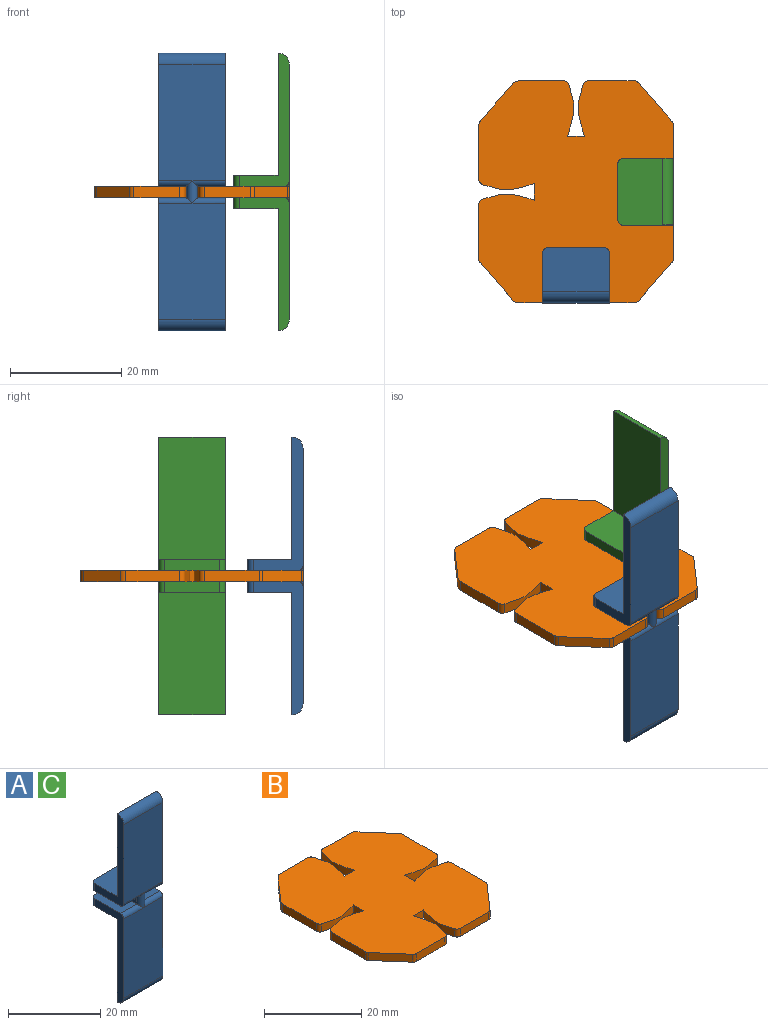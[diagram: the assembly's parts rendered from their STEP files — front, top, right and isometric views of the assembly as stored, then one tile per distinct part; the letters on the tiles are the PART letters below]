
ASSEMBLY  parts=3 mates=2
PART A: 28 faces, bbox 12x10x50 mm
  f0: plane 10x6mm, normal (0,1,0), area 44mm2, adj f2,f4,f5,f8,f10,f17,f18,f19
  f1: plane 21x12mm, normal (0,-1,0), area 252mm2, adj f11,f13,f16,f23,f25
  f2: plane 9x2mm, normal (1,0,0), area 18mm2, adj f0,f4,f8,f15
  f3: plane 21x12mm, normal (0,-1,0), area 252mm2, adj f7,f12,f14,f21,f24
  f4: plane 9x5mm, normal (0,0,-1), area 44.8mm2, adj f0,f2,f7,f14,f18
  f5: plane 12x8mm, normal (0,0,1), area 95.6mm2, adj f0,f6,f7,f18,f21,f27
  f6: plane 22x12mm, normal (0,1,0), area 264mm2, adj f5,f7,f12,f21
  f7: plane 24x9mm, normal (1,0,0), area 60.9mm2, adj f3,f4,f5,f6,f12,f14,f18
  f8: plane 9x5mm, normal (0,0,1), area 44.8mm2, adj f0,f2,f11,f16,f17
  f9: plane 22x12mm, normal (0,1,0), area 264mm2, adj f10,f11,f13,f23
  f10: plane 12x8mm, normal (0,0,-1), area 95.6mm2, adj f0,f9,f11,f17,f23,f26
  f11: plane 24x9mm, normal (1,0,0), area 60.9mm2, adj f1,f8,f9,f10,f13,f16,f17
  f12: cylinder r=2mm len=12mm, axis (-1,0,0), area 37.7mm2, adj f3,f6,f7,f21
  f13: cylinder r=2mm len=12mm, axis (1,0,0), area 37.7mm2, adj f1,f9,f11,f23
  f14: cylinder r=1mm len=6mm, axis (-1,0,0), area 8.4mm2, adj f3,f4,f7,f15
  f15: cylinder r=1mm len=4mm, axis (0,0,1), area 8.6mm2, adj f2,f14,f16,f19,f24,f25
  f16: cylinder r=1mm len=6mm, axis (1,0,0), area 8.4mm2, adj f1,f8,f11,f15
  f17: cylinder r=1mm len=2mm, axis (0,0,-1), area 3.1mm2, adj f0,f8,f10,f11
  f18: cylinder r=1mm len=2mm, axis (0,0,-1), area 3.1mm2, adj f0,f4,f5,f7
  f19: plane 9x2mm, normal (-1,0,0), area 18mm2, adj f0,f15,f20,f22
  f20: plane 9x5mm, normal (0,0,-1), area 44.8mm2, adj f0,f19,f21,f24,f27
  f21: plane 24x9mm, normal (-1,0,0), area 60.9mm2, adj f3,f5,f6,f12,f20,f24,f27
  f22: plane 9x5mm, normal (0,0,1), area 44.8mm2, adj f0,f19,f23,f25,f26
  f23: plane 24x9mm, normal (-1,0,0), area 60.9mm2, adj f1,f9,f10,f13,f22,f25,f26
  f24: cylinder r=1mm len=6mm, axis (1,0,0), area 8.4mm2, adj f3,f15,f20,f21
  f25: cylinder r=1mm len=6mm, axis (-1,0,0), area 8.4mm2, adj f1,f15,f22,f23
  f26: cylinder r=1mm len=2mm, axis (0,0,-1), area 3.1mm2, adj f0,f10,f22,f23
  f27: cylinder r=1mm len=2mm, axis (0,0,-1), area 3.1mm2, adj f0,f5,f20,f21
PART B: 42 faces, bbox 35x40x2 mm
  f0: plane 40x35mm, normal (0,0,-1), area 1233.8mm2, adj f1,f2,f3,f4,f6,f7,f8,f9
  f1: plane 9.85x2mm, normal (1,0,0), area 19.7mm2, adj f0,f5,f17,f36
  f2: plane 8.23x2mm, normal (0,1,0), area 16.5mm2, adj f0,f5,f18,f37
  f3: plane 9.85x2mm, normal (-1,0,0), area 19.7mm2, adj f0,f5,f22,f35
  f4: plane 8.23x2mm, normal (0,-1,0), area 16.5mm2, adj f0,f5,f23,f34
  f5: plane 40x35mm, normal (0,0,1), area 1233.8mm2, adj f1,f2,f3,f4,f6,f7,f8,f9
  f6: plane 9.67x2mm, normal (-1,0,0), area 19.3mm2, adj f0,f5,f12,f41
  f7: extruded ~9.29x2mm, area 19.1mm2, adj f0,f5,f8,f12
  f8: plane 3x2mm, normal (-1,0,0), area 6mm2, adj f0,f5,f7,f19
  f9: plane 3x2mm, normal (0,1,0), area 6mm2, adj f0,f5,f10,f16
  f10: extruded ~9.3x2mm, area 19.1mm2, adj f0,f5,f9,f13
  f11: plane 8x2mm, normal (0,1,0), area 16mm2, adj f0,f5,f13,f40
  f12: cylinder r=1mm len=2mm, axis (0,0,-1), area 2.6mm2, adj f0,f5,f6,f7
  f13: cylinder r=1mm len=2mm, axis (0,0,-1), area 2.5mm2, adj f0,f5,f10,f11
  f14: extruded ~9.29x2mm, area 19.1mm2, adj f0,f5,f15,f17
  f15: plane 3x2mm, normal (1,0,0), area 6mm2, adj f0,f5,f14,f25
  f16: extruded ~9.3x2mm, area 19.1mm2, adj f0,f5,f9,f18
  f17: cylinder r=1mm len=2mm, axis (0,0,-1), area 2.6mm2, adj f0,f1,f5,f14
  f18: cylinder r=1mm len=2mm, axis (0,0,-1), area 2.5mm2, adj f0,f2,f5,f16
  f19: extruded ~9.29x2mm, area 19.1mm2, adj f0,f5,f8,f22
  f20: plane 3x2mm, normal (0,-1,0), area 6mm2, adj f0,f5,f21,f26
  f21: extruded ~9.3x2mm, area 19.1mm2, adj f0,f5,f20,f23
  f22: cylinder r=1mm len=2mm, axis (0,0,-1), area 2.6mm2, adj f0,f3,f5,f19
  f23: cylinder r=1mm len=2mm, axis (0,0,-1), area 2.5mm2, adj f0,f4,f5,f21
  f24: plane 9.85x2mm, normal (1,0,0), area 19.7mm2, adj f0,f5,f28,f39
  f25: extruded ~9.29x2mm, area 19.1mm2, adj f0,f5,f15,f28
  f26: extruded ~9.3x2mm, area 19.1mm2, adj f0,f5,f20,f29
  f27: plane 8.23x2mm, normal (0,-1,0), area 16.5mm2, adj f0,f5,f29,f38
  f28: cylinder r=1mm len=2mm, axis (0,0,-1), area 2.6mm2, adj f0,f5,f24,f25
  f29: cylinder r=1mm len=2mm, axis (0,0,-1), area 2.5mm2, adj f0,f5,f26,f27
  f30: plane 6.9x6.04mm, normal (0.75,-0.66,0), area 18.3mm2, adj f0,f5,f38,f39
  f31: plane 6.59x5.77mm, normal (-0.75,0.66,0), area 17.5mm2, adj f0,f5,f40,f41
  f32: plane 6.9x6.04mm, normal (0.75,0.66,0), area 18.3mm2, adj f0,f5,f36,f37
  f33: plane 6.9x6.04mm, normal (-0.75,-0.66,0), area 18.3mm2, adj f0,f5,f34,f35
  f34: cylinder r=1mm len=2mm, axis (0,0,1), area 1.7mm2, adj f0,f4,f5,f33
  f35: cylinder r=1mm len=2mm, axis (0,0,-1), area 1.4mm2, adj f0,f3,f5,f33
  f36: cylinder r=1mm len=2mm, axis (0,0,1), area 1.4mm2, adj f0,f1,f5,f32
  f37: cylinder r=1mm len=2mm, axis (0,0,-1), area 1.7mm2, adj f0,f2,f5,f32
  f38: cylinder r=1mm len=2mm, axis (0,0,-1), area 1.7mm2, adj f0,f5,f27,f30
  f39: cylinder r=1mm len=2mm, axis (0,0,1), area 1.4mm2, adj f0,f5,f24,f30
  f40: cylinder r=1.5mm len=2mm, axis (0,0,1), area 2.6mm2, adj f0,f5,f11,f31
  f41: cylinder r=1.5mm len=2mm, axis (0,0,-1), area 2.2mm2, adj f0,f5,f6,f31
PART C: same geometry as A
PLACE A rot(axis=(0,-1,0),180deg) t=(-28.62,-40.09,62.79)mm
PLACE B rot(axis=(0,1,0),0deg) t=(2,-28.48,14.3)mm
PLACE C rot(axis=(0.71,-0.71,0),180deg) t=(-15.27,-24.24,62.79)mm
MATE slider A.f0 <-> B.f20  axis (0,1,0) through (-28.62,-34.24,15.3)mm
MATE fastened C.f0 <-> B.f15  axis (-1,0,0) through (-21.12,-24.24,15.3)mm
